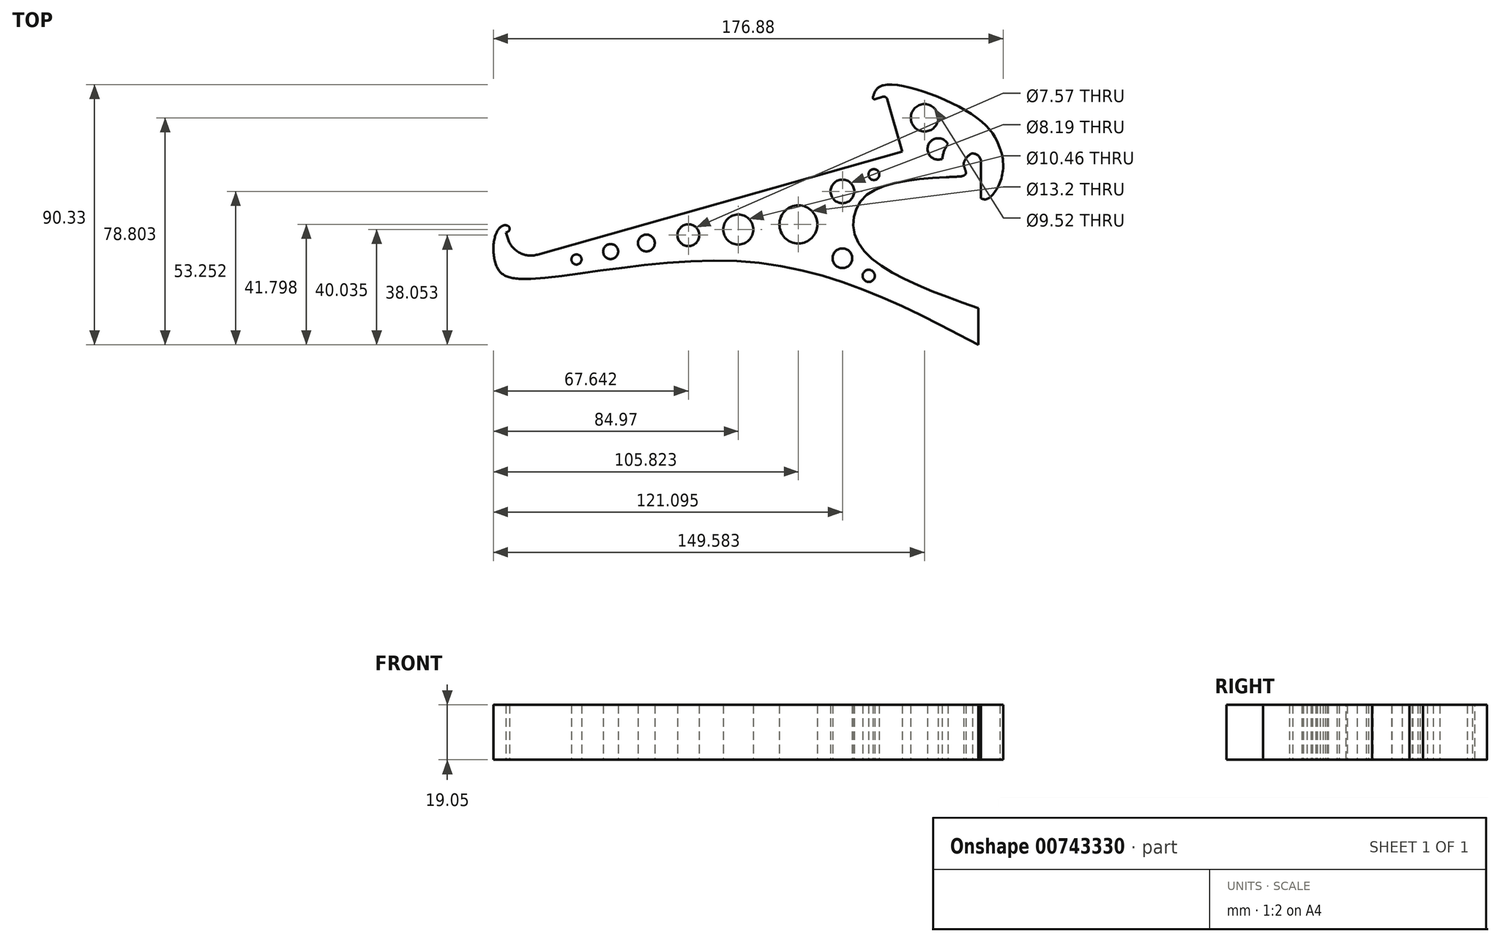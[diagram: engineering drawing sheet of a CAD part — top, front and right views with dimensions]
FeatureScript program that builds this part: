
annotation { "Feature Type Name" : "Feature", "Feature Type Description" : "" }
export const myFeature = defineFeature(function(context is Context, id is Id, definition is map)
    precondition{}
    {
        {
            var Q0;
            Q0=qCreatedBy(makeId("Top.planeOp"),FACE);
            var sketch = newSketch(context, id + "F0", { "sketchPlane" : qUnion([Q0])});
            skCircle(sketch, "E0", {"center": v(0, 0) * mm, "radius": 2.92 * mm});
            skLineSegment(sketch, "E1", {"start": v(2.92, 0) * mm, "end": v(2.92, -12.7) * mm});
            skLineSegment(sketch, "E2", {"start": v(2.92, 0) * mm, "end": v(10.54, 0) * mm});
            skLineSegment(sketch, "E3", {"start": v(2.92, -12.7) * mm, "end": v(5.46, -12.7) * mm});
            skLineSegment(sketch, "E4", {"start": v(5.46, -12.7) * mm, "end": v(10.54, 0) * mm});
            skCircle(sketch, "E5", {"center": v(0, 0) * mm, "radius": 10.54 * mm});
            skLineSegment(sketch, "E6", {"start": v(0, 0) * mm, "end": v(0, 12.7) * mm});
            skLineSegment(sketch, "E7", {"start": v(0, 10.54) * mm, "end": v(-134.62, 10.54) * mm});
            skLineSegment(sketch, "E8", {"start": v(-134.62, 10.54) * mm, "end": v(-134.62, -27.56) * mm});
            skLineSegment(sketch, "E9", {"start": v(-134.62, -27.56) * mm, "end": v(0, 10.54) * mm});
            skLineSegment(sketch, "E10", {"start": v(-38.58, -0.38) * mm, "end": v(-43.3, 16.3) * mm});
            skLineSegment(sketch, "E11", {"start": v(0, 10.54) * mm, "end": v(-24.44, 3.62) * mm});
            skLineSegment(sketch, "E12", {"start": v(-24.44, 3.62) * mm, "end": v(-29.9, 22.93) * mm});
            skLineSegment(sketch, "E13", {"start": v(-29.9, 22.93) * mm, "end": v(-34.8, 21.55) * mm});
            skLineSegment(sketch, "E14", {"start": v(-134.62, -27.56) * mm, "end": v(-159.06, -34.48) * mm});
            skLineSegment(sketch, "E15", {"start": v(-159.06, -34.48) * mm, "end": v(-161.9, -24.46) * mm});
            skLineSegment(sketch, "E16", {"start": v(-159.06, -34.48) * mm, "end": v(-165.17, -36.2) * mm});
            skLineSegment(sketch, "E17", {"start": v(-159.06, -34.48) * mm, "end": v(-157.33, -40.59) * mm});
            skLineSegment(sketch, "E18", {"start": v(2.92, -12.7) * mm, "end": v(2.92, -50.8) * mm});
            skLineSegment(sketch, "E19", {"start": v(2.92, -50.8) * mm, "end": v(2.08, -50.8) * mm});
            skLineSegment(sketch, "E20", {"start": v(2.08, -50.8) * mm, "end": v(2.08, -63.5) * mm});
            skFitSpline(sketch, "E21", {"points": [v(2.08, -50.8) * mm, v(-39.32, -28.6) * mm, v(-37.47, -12.18) * mm, v(-4.12, -5.08) * mm], "startDerivative": vector(-131.71, 46.56) * mm, "endDerivative": vector(116.62, 5.1) * mm});
            skLineSegment(sketch, "E22", {"start": v(-29.9, 22.93) * mm, "end": v(-30.94, 26.6) * mm});
            skFitSpline(sketch, "E23", {"points": [v(-34.8, 21.55) * mm, v(-30.94, 26.6) * mm, v(3.16, 14) * mm, v(10.54, 0) * mm], "startDerivative": vector(8.25, 32.67) * mm, "endDerivative": vector(8.6, -44.05) * mm});
            skCircle(sketch, "E24", {"center": v(-60.43, -21.7) * mm, "radius": 6.6 * mm});
            skCircle(sketch, "E25", {"center": v(-81.28, -23.46) * mm, "radius": 5.23 * mm});
            skCircle(sketch, "E26", {"center": v(-16.67, 15.3) * mm, "radius": 4.76 * mm});
            skCircle(sketch, "E27", {"center": v(-45.16, -33.45) * mm, "radius": 3.43 * mm});
            skCircle(sketch, "E28", {"center": v(-45.16, -10.25) * mm, "radius": 4.1 * mm});
            skCircle(sketch, "E29", {"center": v(-98.6, -25.45) * mm, "radius": 3.78 * mm});
            skFitSpline(sketch, "E30", {"points": [v(10.54, 0) * mm, v(5.46, -12.7) * mm, v(2.92, -12.7) * mm], "startDerivative": vector(3.05, -24.78) * mm, "endDerivative": vector(-8.6, 2.74) * mm});
            skCircle(sketch, "E31", {"center": v(-113.18, -28.16) * mm, "radius": 2.9 * mm});
            skCircle(sketch, "E32", {"center": v(-125.57, -31.13) * mm, "radius": 2.62 * mm});
            skCircle(sketch, "E33", {"center": v(-11.89, 4.5) * mm, "radius": 3.71 * mm});
            skLineSegment(sketch, "E34", {"start": v(-161.9, -24.46) * mm, "end": v(-159.2, -23.7) * mm});
            skLineSegment(sketch, "E35", {"start": v(-161.9, -24.46) * mm, "end": v(-162.59, -22.01) * mm});
            skLineSegment(sketch, "E36", {"start": v(-161.9, -24.46) * mm, "end": v(-165.56, -25.5) * mm});
            skFitSpline(sketch, "E37", {"points": [v(-159.2, -23.7) * mm, v(-162.59, -22.01) * mm, v(-165.56, -25.5) * mm, v(-165.17, -36.2) * mm, v(-157.33, -40.59) * mm, v(-81.05, -34.48) * mm, v(2.08, -63.5) * mm], "startDerivative": vector(-64.54, 54.37) * mm, "endDerivative": vector(241.92, -127.04) * mm});
            skLineSegment(sketch, "E38", {"start": v(-2.38, -1.69) * mm, "end": v(-2.38, -4.23) * mm});
            skFitSpline(sketch, "E39", {"points": [v(-4.12, -5.08) * mm, v(-2.38, -4.23) * mm, v(-2.75, -2.15) * mm, v(-2.92, 0) * mm, v(0, 2.92) * mm, v(2.05, -1.1) * mm], "startDerivative": vector(13.76, 3.28) * mm, "endDerivative": vector(6.08, -23.8) * mm});
            skCircle(sketch, "E40", {"center": v(-137.44, -33.88) * mm, "radius": 1.76 * mm});
            skCircle(sketch, "E41", {"center": v(-34.23, -4.42) * mm, "radius": 1.88 * mm});
            skCircle(sketch, "E42", {"center": v(-36.03, -39.56) * mm, "radius": 2.12 * mm});
            skSolve(sketch);
        }
        {
            var Q0;
            {var subQ0=sQuery(id+"F0.wireOp",EDGE,"E13");Q0=makeQuery(id+"F0.imprint","IMPRINT",FACE,{"disambiguationData":[TD([[makeQuery(id+"F0.imprint","IMPRINT",EDGE,{"derivedFrom":subQ0}),-1.0]])]});}
            var Q1;
            {var subQ0=sQuery(id+"F0.wireOp",EDGE,"E22");Q1=makeQuery(id+"F0.imprint","IMPRINT",FACE,{"disambiguationData":[TD([[makeQuery(id+"F0.imprint","IMPRINT",EDGE,{"derivedFrom":subQ0}),-1.0]])]});}
            var Q2;
            {var subQ0=sQuery(id+"F0.wireOp",EDGE,"E7");var subQ1=makeQuery(id+"F0.imprint","INTERSECT",VERTEX,{"derivedFrom":[subQ0,sQuery(id+"F0.wireOp",EDGE,"E26")]});Q2=makeQuery(id+"F0.imprint","IMPRINT",FACE,{"disambiguationData":[TD([[makeQuery(id+"F0.imprint","IMPRINT",EDGE,{"disambiguationData":[TD([[subQ1,-1.0]])],"derivedFrom":subQ0}),1.0]])]});}
            var Q3;
            {var subQ0=sQuery(id+"F0.wireOp",EDGE,"E15");Q3=makeQuery(id+"F0.imprint","IMPRINT",FACE,{"disambiguationData":[TD([[makeQuery(id+"F0.imprint","IMPRINT",EDGE,{"derivedFrom":subQ0}),1.0]])]});}
            var Q4;
            {var subQ0=sQuery(id+"F0.wireOp",EDGE,"E16");Q4=makeQuery(id+"F0.imprint","IMPRINT",FACE,{"disambiguationData":[TD([[makeQuery(id+"F0.imprint","IMPRINT",EDGE,{"derivedFrom":subQ0}),1.0]])]});}
            var Q5;
            {var subQ6=sQuery(id+"F0.wireOp",EDGE,"E14");Q5=makeQuery(id+"F0.imprint","IMPRINT",FACE,{"disambiguationData":[TD([[makeQuery(id+"F0.imprint","IMPRINT",EDGE,{"derivedFrom":subQ6}),1.0]])]});}
            var Q6;
            {var subQ7=sQuery(id+"F0.wireOp",EDGE,"cUOpIUV0-puMu-mCj6-igYg-XsSuG1bvqNPG");Q6=makeQuery(id+"F0.imprint","IMPRINT",FACE,{"disambiguationData":[TD([[makeQuery(id+"F0.imprint","IMPRINT",EDGE,{"derivedFrom":subQ7}),-1.0]])]});}
            var Q7;
            {var subQ5=sQuery(id+"F0.wireOp",EDGE,"E2");Q7=makeQuery(id+"F0.imprint","IMPRINT",FACE,{"disambiguationData":[TD([[makeQuery(id+"F0.imprint","IMPRINT",EDGE,{"derivedFrom":subQ5}),1.0]])]});}
            var Q8;
            {var subQ0=sQuery(id+"F0.wireOp",EDGE,"E2");Q8=makeQuery(id+"F0.imprint","IMPRINT",FACE,{"disambiguationData":[TD([[makeQuery(id+"F0.imprint","IMPRINT",EDGE,{"derivedFrom":subQ0}),-1.0]])]});}
            var Q9;
            {var subQ0=sQuery(id+"F0.wireOp",EDGE,"E11");var subQ1=sQuery(id+"F0.wireOp",EDGE,"E5");var subQ3=makeQuery(id+"F0.imprint","INTERSECT",VERTEX,{"derivedFrom":[subQ1,subQ0]});Q9=makeQuery(id+"F0.imprint","IMPRINT",FACE,{"disambiguationData":[TD([[makeQuery(id+"F0.imprint","IMPRINT",EDGE,{"disambiguationData":[TD([[subQ3,1.0]])],"derivedFrom":subQ1}),1.0]])]});}
            var Q10;
            {var subQ0=sQuery(id+"F0.wireOp",EDGE,"E5");var subQ1=sQuery(id+"F0.wireOp",EDGE,"E4");var subQ3=makeQuery(id+"F0.imprint","INTERSECT",VERTEX,{"derivedFrom":[subQ1,subQ0]});Q10=makeQuery(id+"F0.imprint","IMPRINT",FACE,{"disambiguationData":[TD([[makeQuery(id+"F0.imprint","IMPRINT",EDGE,{"disambiguationData":[TD([[subQ3,-1.0]])],"derivedFrom":subQ1}),-1.0]])]});}
            var Q11;
            {var subQ1=sQuery(id+"F0.wireOp",EDGE,"E4");var subQ3=sQuery(id+"F0.wireOp",EDGE,"E5");var subQ4=makeQuery(id+"F0.imprint","INTERSECT",VERTEX,{"derivedFrom":[subQ1,subQ3]});Q11=makeQuery(id+"F0.imprint","IMPRINT",FACE,{"disambiguationData":[TD([[makeQuery(id+"F0.imprint","IMPRINT",EDGE,{"disambiguationData":[TD([[subQ4,1.0]])],"derivedFrom":subQ1}),-1.0]])]});}
            var Q12;
            {var subQ1=sQuery(id+"F0.wireOp",EDGE,"E3");Q12=makeQuery(id+"F0.imprint","IMPRINT",FACE,{"disambiguationData":[TD([[makeQuery(id+"F0.imprint","IMPRINT",EDGE,{"derivedFrom":subQ1}),1.0]])]});}
            var Q13;
            {var subQ0=sQuery(id+"F0.wireOp",EDGE,"E3");Q13=makeQuery(id+"F0.imprint","IMPRINT",FACE,{"disambiguationData":[TD([[makeQuery(id+"F0.imprint","IMPRINT",EDGE,{"derivedFrom":subQ0}),-1.0]])]});}
            var Q14;
            {var subQ0=sQuery(id+"F0.wireOp",EDGE,"E11");var subQ1=sQuery(id+"F0.wireOp",EDGE,"E5");var subQ2=makeQuery(id+"F0.imprint","INTERSECT",VERTEX,{"derivedFrom":[subQ1,subQ0]});Q14=makeQuery(id+"F0.imprint","IMPRINT",FACE,{"disambiguationData":[TD([[makeQuery(id+"F0.imprint","IMPRINT",EDGE,{"disambiguationData":[TD([[subQ2,-1.0]])],"derivedFrom":subQ1}),-1.0]])]});}
            var Q15;
            {var subQ0=sQuery(id+"F0.wireOp",EDGE,"E35");Q15=makeQuery(id+"F0.imprint","IMPRINT",FACE,{"disambiguationData":[TD([[makeQuery(id+"F0.imprint","IMPRINT",EDGE,{"derivedFrom":subQ0}),1.0]])]});}
            var Q16;
            {var subQ0=sQuery(id+"F0.wireOp",EDGE,"E34");Q16=makeQuery(id+"F0.imprint","IMPRINT",FACE,{"disambiguationData":[TD([[makeQuery(id+"F0.imprint","IMPRINT",EDGE,{"derivedFrom":subQ0}),1.0]])]});}
            var Q17;
            {var subQ0=sQuery(id+"F0.wireOp",EDGE,"E39");var subQ15=sQuery(id+"F0.wireOp",EDGE,"E0");var subQ17=makeQuery(id+"F0.imprint","INTERSECT",VERTEX,{"disambiguationData":[OD(0.0)],"derivedFrom":[subQ15,subQ0]});Q17=makeQuery(id+"F0.imprint","IMPRINT",FACE,{"disambiguationData":[TD([[makeQuery(id+"F0.imprint","IMPRINT",EDGE,{"disambiguationData":[TD([[subQ17,-1.0]])],"derivedFrom":subQ15}),-1.0]])]});}
            var Q18;
            {var subQ0=sQuery(id+"F0.wireOp",EDGE,"E39");var subQ1=sQuery(id+"F0.wireOp",EDGE,"E0");var subQ2=makeQuery(id+"F0.imprint","INTERSECT",VERTEX,{"disambiguationData":[OD(0.0)],"derivedFrom":[subQ1,subQ0]});Q18=makeQuery(id+"F0.imprint","IMPRINT",FACE,{"disambiguationData":[TD([[makeQuery(id+"F0.imprint","IMPRINT",EDGE,{"disambiguationData":[TD([[subQ2,-1.0]])],"derivedFrom":subQ1}),1.0]])]});}
            var Q19;
            {var subQ0=sQuery(id+"F0.wireOp",EDGE,"E39");var subQ1=sQuery(id+"F0.wireOp",EDGE,"E38");var subQ2=makeQuery(id+"F0.imprint","INTERSECT",VERTEX,{"disambiguationData":[OD(0.0)],"derivedFrom":[subQ1,subQ0]});Q19=makeQuery(id+"F0.imprint","IMPRINT",FACE,{"disambiguationData":[TD([[makeQuery(id+"F0.imprint","IMPRINT",EDGE,{"disambiguationData":[TD([[subQ2,1.0]])],"derivedFrom":subQ1}),1.0]])]});}
            extrude(context, id + "F1", {"entities" : qUnion([Q0, Q1, Q2, Q3, Q4, Q5, Q6, Q7, Q8, Q9, Q10, Q11, Q12, Q13, Q14, Q15, Q16, Q17, Q18, Q19]), "depth" : 19.05 * mm, "offsetDistance" : 25.4 * mm});
        }
        {
            var Q0;
            Q0=makeQuery(id+"F1.opExtrude","SWEPT_EDGE",EDGE,{"disambiguationData":[OSD([sQuery(id+"F0.wireOp",EDGE,"E14"),sQuery(id+"F0.wireOp",EDGE,"E15"),sQuery(id+"F0.wireOp",EDGE,"E16"),sQuery(id+"F0.wireOp",EDGE,"E17")])]});
            fillet(context, id + "F2", {"entities" : qUnion([Q0]), "radius" : 8.38 * mm, "tangentPropagation" : true, "allowEdgeOverflow" : false});
        }
        {
            var Q0;
            Q0=makeQuery(id+"F1.opExtrude","SWEPT_EDGE",EDGE,{"disambiguationData":[OSD([sQuery(id+"F0.wireOp",EDGE,"E12"),sQuery(id+"F0.wireOp",EDGE,"E13"),sQuery(id+"F0.wireOp",EDGE,"E22")])]});
            fillet(context, id + "F3", {"entities" : qUnion([Q0]), "radius" : 1.27 * mm, "tangentPropagation" : true, "allowEdgeOverflow" : false});
        }
        {
            var Q0;
            Q0=makeQuery(id+"F1.opExtrude","SWEPT_EDGE",EDGE,{"disambiguationData":[OSD([sQuery(id+"F0.wireOp",EDGE,"E13"),sQuery(id+"F0.wireOp",EDGE,"E23")])]});
            fillet(context, id + "F4", {"entities" : qUnion([Q0]), "radius" : 0.5 * mm, "tangentPropagation" : true, "allowEdgeOverflow" : false});
        }
        {
            var Q0;
            Q0=makeQuery(id+"F1.opExtrude","SWEPT_EDGE",EDGE,{"disambiguationData":[OSD([sQuery(id+"F0.wireOp",EDGE,"cUOpIUV0-puMu-mCj6-igYg-XsSuG1bvqNPG"),sQuery(id+"F0.wireOp",EDGE,"E21")])]});
            fillet(context, id + "F5", {"entities" : qUnion([Q0]), "radius" : 2.54 * mm, "tangentPropagation" : true, "allowEdgeOverflow" : false});
        }
        {
            var Q0;
            Q0=makeQuery(id+"F1.opExtrude","SWEPT_EDGE",EDGE,{"disambiguationData":[OSD([sQuery(id+"F0.wireOp",EDGE,"E34"),sQuery(id+"F0.wireOp",EDGE,"E37")])]});
            fillet(context, id + "F6", {"entities" : qUnion([Q0]), "radius" : 1.14 * mm, "tangentPropagation" : true, "allowEdgeOverflow" : false});
        }
    });
